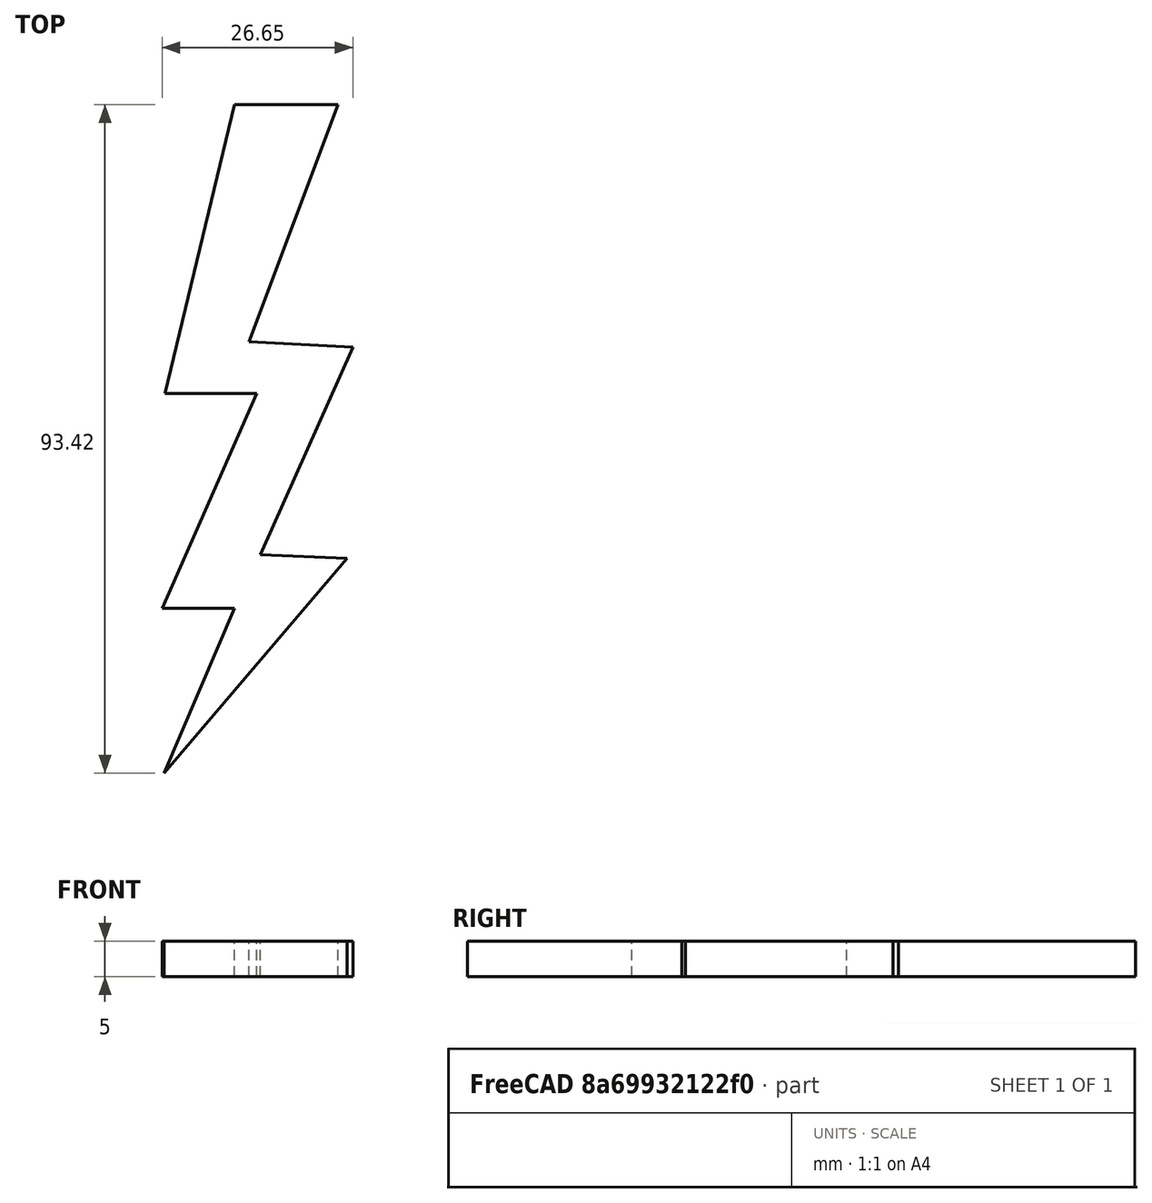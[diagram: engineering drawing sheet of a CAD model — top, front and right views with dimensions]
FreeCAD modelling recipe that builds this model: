
FCSTD DOCUMENT  (FreeCAD 0.21R33694 (Git))
Label: OJT1_T16R03_llampec
License: All rights reserved
LicenseURL: https://en.wikipedia.org/wiki/All_rights_reserved
objects: Sketcher::SketchObject×1, PartDesign::Pad×1, PartDesign::Body×1
note: 4 computed .brp shape members not serialized (recipe doc carries the construction recipe); baked Part::Feature solids carry a one-line shape summary decoded from their .brp

FEATURE [Sketcher::SketchObject] Sketch  label="raig"
  FullyConstrained = false
  MapMode = 5
  Support = -> [XY_Plane]
  sketch-geometry (11):
    g0: LineSegment StartX=10.1695 StartY=9.88897 StartZ=0 EndX=19.8625 EndY=50.2574 EndZ=0
    g1: LineSegment StartX=19.8625 StartY=50.2574 StartZ=0 EndX=34.3537 EndY=50.2574 EndZ=0
    g2: LineSegment StartX=34.3537 StartY=50.2574 StartZ=0 EndX=21.9327 EndY=17.1346 EndZ=0
    g3: LineSegment StartX=21.9327 StartY=17.1346 StartZ=0 EndX=36.4239 EndY=16.3583 EndZ=0
    g4: LineSegment StartX=36.4239 StartY=16.3583 StartZ=0 EndX=23.4853 EndY=-12.6242 EndZ=0
    g5: LineSegment StartX=23.4853 StartY=-12.6242 StartZ=0 EndX=35.6476 EndY=-13.1417 EndZ=0
    g6: LineSegment StartX=35.6476 StartY=-13.1417 StartZ=0 EndX=10.0292 EndY=-43.1592 EndZ=0
    g7: LineSegment StartX=10.0292 StartY=-43.1592 StartZ=0 EndX=19.8625 EndY=-20.1286 EndZ=0
    g8: LineSegment StartX=19.8625 StartY=-20.1286 StartZ=0 EndX=9.77043 EndY=-20.1286 EndZ=0
    g9: LineSegment StartX=9.77043 StartY=-20.1286 StartZ=0 EndX=22.9678 EndY=9.88897 EndZ=0
    g10: LineSegment StartX=22.9678 StartY=9.88897 StartZ=0 EndX=10.1695 EndY=9.88897 EndZ=0
  constraints (14):
    c: Coincident(g0,g1)
    c: Horizontal(g1)
    c: Coincident(g1,g2)
    c: Coincident(g2,g3)
    c: Coincident(g3,g4)
    c: Coincident(g4,g5)
    c: Coincident(g5,g6)
    c: Coincident(g6,g7)
    c: Coincident(g7,g8)
    c: Horizontal(g8)
    c: Coincident(g8,g9)
    c: Coincident(g9,g10)
    c: Coincident(g10,g0)
    c: Horizontal(g10)
FEATURE [PartDesign::Pad] Pad  label="LLAMPEC"
  Direction = (0,0,1)
  Length = 5
  Length2 = 10
  Profile = -> Sketch
  ReferenceAxis = -> Sketch [N_Axis]
  Type = 0
FEATURE [PartDesign::Body] Body
  Group = -> [Sketch,Pad]
  Origin = -> Origin
  Tip = -> Pad
